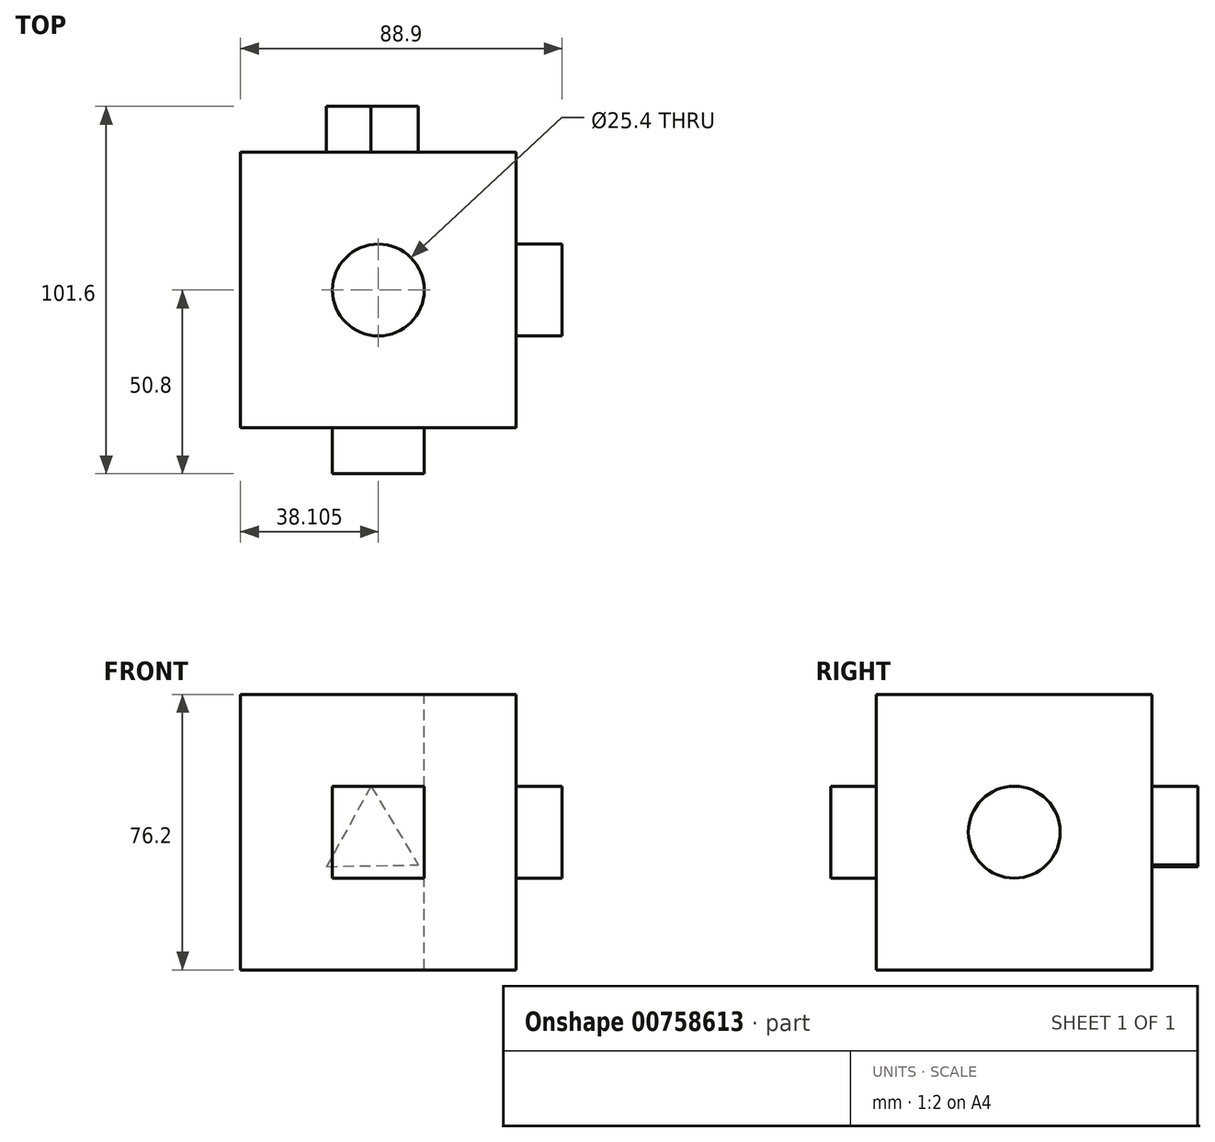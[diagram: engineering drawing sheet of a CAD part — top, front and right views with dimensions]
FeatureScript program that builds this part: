
annotation { "Feature Type Name" : "Feature", "Feature Type Description" : "" }
export const myFeature = defineFeature(function(context is Context, id is Id, definition is map)
    precondition{}
    {
        {
            var Q0;
            Q0=qCreatedBy(makeId("Front.planeOp"),FACE);
            var sketch = newSketch(context, id + "F0", { "sketchPlane" : qUnion([Q0])});
            skLineSegment(sketch, "E0.bottom", {"start": v(-22.2, 0) * mm, "end": v(54, 0) * mm});
            skLineSegment(sketch, "E0.top", {"start": v(-22.2, 76.2) * mm, "end": v(54, 76.2) * mm});
            skLineSegment(sketch, "E0.left", {"start": v(-22.2, 0) * mm, "end": v(-22.2, 76.2) * mm});
            skLineSegment(sketch, "E0.right", {"start": v(54, 0) * mm, "end": v(54, 76.2) * mm});
            skSolve(sketch);
        }
        {
            var Q0;
            Q0=makeQuery(id+"F0.imprint","IMPRINT",FACE,{"disambiguationData":[TD([[makeQuery(id+"F0.imprint","IMPRINT",EDGE,{"derivedFrom":sQuery(id+"F0.wireOp",EDGE,"E0.bottom")}),1.0]])]});
            extrude(context, id + "F1", {"entities" : qUnion([Q0]), "depth" : 76.2 * mm, "offsetDistance" : 25.4 * mm});
        }
        {
            var Q0;
            Q0=makeQuery(id+"F1.opExtrude","CAP_FACE",FACE,{"disambiguationData":[OSD([sQuery(id+"F0.wireOp",EDGE,"E0.bottom"),sQuery(id+"F0.wireOp",EDGE,"E0.top"),sQuery(id+"F0.wireOp",EDGE,"E0.left"),sQuery(id+"F0.wireOp",EDGE,"E0.right")])],"isStart":false});
            var sketch = newSketch(context, id + "F2", { "sketchPlane" : qUnion([Q0])});
            skLineSegment(sketch, "E1.bottom", {"start": v(3.2, 50.8) * mm, "end": v(28.6, 50.8) * mm});
            skLineSegment(sketch, "E1.top", {"start": v(3.2, 25.4) * mm, "end": v(28.6, 25.4) * mm});
            skLineSegment(sketch, "E1.left", {"start": v(3.2, 50.8) * mm, "end": v(3.2, 25.4) * mm});
            skLineSegment(sketch, "E1.right", {"start": v(28.6, 50.8) * mm, "end": v(28.6, 25.4) * mm});
            skSolve(sketch);
        }
        {
            var Q0;
            Q0=makeQuery(id+"F2.imprint","IMPRINT",FACE,{"disambiguationData":[TD([[makeQuery(id+"F2.imprint","IMPRINT",EDGE,{"derivedFrom":sQuery(id+"F2.wireOp",EDGE,"E1.bottom")}),-1.0]])]});
            extrude(context, id + "F3", {"entities" : qUnion([Q0]), "operationType" : NewBodyOperationType.ADD, "depth" : 12.7 * mm, "offsetDistance" : 25.4 * mm});
        }
        {
            var Q0;
            Q0=makeQuery(id+"F1.opExtrude","SWEPT_FACE",FACE,{"disambiguationData":[OSD([sQuery(id+"F0.wireOp",EDGE,"E0.right")])]});
            var sketch = newSketch(context, id + "F4", { "sketchPlane" : qUnion([Q0])});
            skCircle(sketch, "E2", {"center": v(-38.1, 38.1) * mm, "radius": 12.7 * mm});
            skSolve(sketch);
        }
        {
            var Q0;
            Q0=makeQuery(id+"F4.imprint","IMPRINT",FACE,{"disambiguationData":[TD([[makeQuery(id+"F4.imprint","IMPRINT",EDGE,{"derivedFrom":sQuery(id+"F4.wireOp",EDGE,"E2")}),1.0]])]});
            extrude(context, id + "F5", {"entities" : qUnion([Q0]), "operationType" : NewBodyOperationType.ADD, "depth" : 12.7 * mm, "offsetDistance" : 25.4 * mm});
        }
        {
            var Q0;
            Q0=makeQuery(id+"F1.opExtrude","SWEPT_FACE",FACE,{"disambiguationData":[OSD([sQuery(id+"F0.wireOp",EDGE,"E0.top")])]});
            var sketch = newSketch(context, id + "F6", { "sketchPlane" : qUnion([Q0])});
            skPoint(sketch, "E3", {"position": v(15.9, -38.1) * mm});
            skSolve(sketch);
        }
        {
            var Q0;
            Q0=sQuery(id+"F6.wireOp",VERTEX,"E3");
            var Q1;
            Q1=makeQuery(id+"F1.opExtrude","SWEPT_BODY",BODY,{"disambiguationData":[OSD([sQuery(id+"F0.wireOp",EDGE,"E0.bottom"),sQuery(id+"F0.wireOp",EDGE,"E0.top"),sQuery(id+"F0.wireOp",EDGE,"E0.left"),sQuery(id+"F0.wireOp",EDGE,"E0.right")])]});
            hole(context, id + "F7", {"style" : HoleStyle.SIMPLE, "endStyle" : HoleEndStyle.THROUGH, "holeDiameter" : 25.4 * mm, "majorDiameter" : 6.35 * mm, "isTappedThrough" : true, "tappedDepth" : 12.7 * mm, "tapClearance" : 3, "locations" : qUnion([Q0]), "scope" : qUnion([Q1])});
        }
        {
            var Q0;
            Q0=makeQuery(id+"F1.opExtrude","CAP_FACE",FACE,{"disambiguationData":[OSD([sQuery(id+"F0.wireOp",EDGE,"E0.bottom"),sQuery(id+"F0.wireOp",EDGE,"E0.top"),sQuery(id+"F0.wireOp",EDGE,"E0.left"),sQuery(id+"F0.wireOp",EDGE,"E0.right")])],"isStart":true});
            var sketch = newSketch(context, id + "F8", { "sketchPlane" : qUnion([Q0])});
            skLineSegment(sketch, "E4", {"start": v(-13.88, 50.8) * mm, "end": v(-26.96, 29.03) * mm});
            skLineSegment(sketch, "E5", {"start": v(-13.88, 50.8) * mm, "end": v(-1.56, 28.58) * mm});
            skLineSegment(sketch, "E6", {"start": v(-1.56, 28.58) * mm, "end": v(-26.96, 29.03) * mm});
            skSolve(sketch);
        }
        {
            var Q0;
            Q0=makeQuery(id+"F8.imprint","IMPRINT",FACE,{"disambiguationData":[TD([[makeQuery(id+"F8.imprint","IMPRINT",EDGE,{"derivedFrom":sQuery(id+"F8.wireOp",EDGE,"E4")}),1.0]])]});
            extrude(context, id + "F9", {"entities" : qUnion([Q0]), "operationType" : NewBodyOperationType.ADD, "depth" : 12.7 * mm, "offsetDistance" : 25.4 * mm});
        }
    });
